# Revit family: Domotics-DomesticRanges-GEWISS-CHORUS_DATA-SOCKET-OUTLET_RJ45
name_source: partatom
category: Apparecchi elettrici
revit_build: Autodesk Revit 2016 (Build: 20161004_0715(x64)
units: mm (PartAtom-declared; Revit-internal decimal feet)

## family parameters
Condiviso = Sì
Host = Superficie
Mantenere orientamento annotazione = Sì
Numero OmniClass = 23.80.50.14
Punto di calcolo locali = Sì
Quota connettore circolare = Usa diametro
Taglio con vuoti quando caricato = Sì
Tipo di parte = Normale
Titolo OmniClass = Plug Connectors

## types (12) — shared parameters
Catalogue = DOMOTICS
Catalogue Range = CHORUS - DOMESTIC RANGE
GW - Testo elettrico = RJ45
IDF = 1a8bcbcc-4c0f-486d-ade8-be7f6039fe1c
IDT = e3484578-d4ee-4f41-a417-bd6924481e09
Immagine tipo = GW14421.jpg
Larghezza presa = 23 mm  [stored 0.0754593 ft]
Produttore = GEWISS S.p.A.
Prospetto di default = 1219 mm
Simbolo = SIMBOLO PRESE TELEFONO : PRESA TEL
Technical sheet = https://www.gewiss.com
Tipo = SYSTEM PRESE RJ45_BASE : RJ45 Titanio
URL = https://www.gewiss.com
Version file RFA = 19.0

## per-type parameters (varying)
| type | Cables | Category | Colour | Connection | Description. | Description: | Descrizione | EAN code | Electrocod | Modello | No. Chorus modules: | No. SYSTEM modules | No. pairs | Number pairs | SEO | Standard; | Use category |
| GW10424 - CONNECTOR RJ45 1M CAT.6 FTP CHORUS W | FTP | Data socket | White | Toolless | Data socket | RJ45 | CONNECTOR RJ45 1M CAT.6 FTP CHORUS W | 8011564257702 | 3722 | GW10424 | 1 | 1 | 4 | 4 | Socket outlet | EN 60603-7-5 | 6 |
| GW12422 - CONNECTOR RJ45 1M CAT.5E FTP CHORUS B |  |  |  |  |  |  | CONNECTOR RJ45 1M CAT.5E FTP CHORUS B | 8011564269118 | 0130 | GW12422 |  |  |  |  |  |  |  |
| GW12424 - CONNECTOR RJ45 1M CAT.6 FTP CHORUS B |  |  |  |  |  |  | CONNECTOR RJ45 1M CAT.6 FTP CHORUS B | 8011564269132 | 0131 | GW12424 |  |  |  |  |  |  |  |
| GW12421 - CONNECTOR RJ45 1M CAT.5E UTP CHORUS B |  |  |  |  |  |  | CONNECTOR RJ45 1M CAT.5E UTP CHORUS B | 8011564269101 | 0131 | GW12421 |  |  |  |  |  |  |  |
| GW10421 - CONNECTOR RJ45 1M CAT.5E UTP CHORUS W | UTP | Data socket | White | Toolless | Data socket | RJ45 | CONNECTOR RJ45 1M CAT.5E UTP CHORUS W | 8011564257672 | 3722 | GW10421 | 1 | 1 | 4 | 4 | Socket outlet | EN 60603-7-2 | 5e |
| GW10422 - CONNECTOR RJ45 1M CAT.5E FTP CHORUS W | FTP | Data socket | White | Toolless | Data socket | RJ45 | CONNECTOR RJ45 1M CAT.5E FTP CHORUS W | 8011564257689 | 3722 | GW10422 | 1 | 1 | 4 | 4 | Socket outlet | EN 60603-7-3 | 5e |
| GW10423 - CONNECTOR RJ45 1M CAT.6 UTP CHORUS W | UTP | Data socket | White | Toolless | Data socket | RJ45 | CONNECTOR RJ45 1M CAT.6 UTP CHORUS W | 8011564257696 | 3722 | GW10423 | 1 | 1 | 4 | 4 | Socket outlet | EN 60603-7-4 | 6 |
| GW12423 - CONNECTOR RJ45 1M CAT.6 UTP CHORUS B |  |  |  |  |  |  | CONNECTOR RJ45 1M CAT.6 UTP CHORUS B | 8011564269125 | 0130 | GW12423 |  |  |  |  |  |  |  |
| GW14423 - CONNECTOR RJ45 1M CAT.6 UTP CHORUS T |  |  |  |  |  |  | CONNECTOR RJ45 1M CAT.6 UTP CHORUS T | 8011564267299 | 0131 | GW14423 |  |  |  |  |  |  |  |
| GW14421 - CONNECTOR RJ45 1M CAT.5E UTP CHORUS T |  |  |  |  |  |  | CONNECTOR RJ45 1M CAT.5E UTP CHORUS T | 8011564267268 | 0131 | GW14421 |  |  |  |  |  |  |  |
| GW14422 - CONNECTOR RJ45 1M CAT.5E FTP CHORUS T |  |  |  |  |  |  | CONNECTOR RJ45 1M CAT.5E FTP CHORUS T | 8011564267275 | 0131 | GW14422 |  |  |  |  |  |  |  |
| GW14424 - CONNECTOR RJ45 1M CAT.6 FTP CHORUS T |  |  |  |  |  |  | CONNECTOR RJ45 1M CAT.6 FTP CHORUS T | 8011564267305 | 0131 | GW14424 |  |  |  |  |  |  |  |

note: [stored X ft] marks values corroborated as IEEE doubles in the binary element streams (Revit-internal decimal feet)

## geometry (parser evidence)
native form markers: Sweep x1
no freeform markers — native parametric forms only
